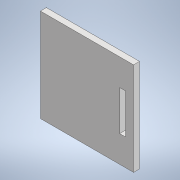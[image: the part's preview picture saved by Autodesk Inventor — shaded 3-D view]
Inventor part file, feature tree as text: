
AUTODESK INVENTOR PART (.ipt)
format: ipt  version: 2022.3 (Build 263350000, 350)  size: 107,520 bytes
history: native  units: mm
features: other x8, reference x6, extrude x1, sketch x1
ambient origin geometry x8: Origin, YZ Plane, XZ Plane, XY Plane, X Axis, Y Axis, Z Axis, Center Point
bodies: Solid1 (feature_tree)
feature tree (16):
  extrude  "Extrusion1"  Depth=25.0mm
  sketch  "Sketch1"  dims[d2=23.962763mm d3=25.0mm d4=12.5mm d5=5.35mm d6=1.6mm d7=0.0mm]
  reference  "Reference1"
  reference  "Reference2"
  reference  "Reference3"
  reference  "Reference4"
  reference  "Reference5"
  reference  "Reference6"
  other  "<userpath>\Documents\Inventor\NanoSumo\Przekładnia.iam"
  other  "Przekładnia.iam"
  other  "silnik_2:3"
  other  "Spur Gears:2"
  other  "Spur Gear2:1"
  other  "Spur Gears2_MIR1:1"
  other  "Spur Gear22_MIR1:1"
  other  "TOF_VL53L0X (1):1"
